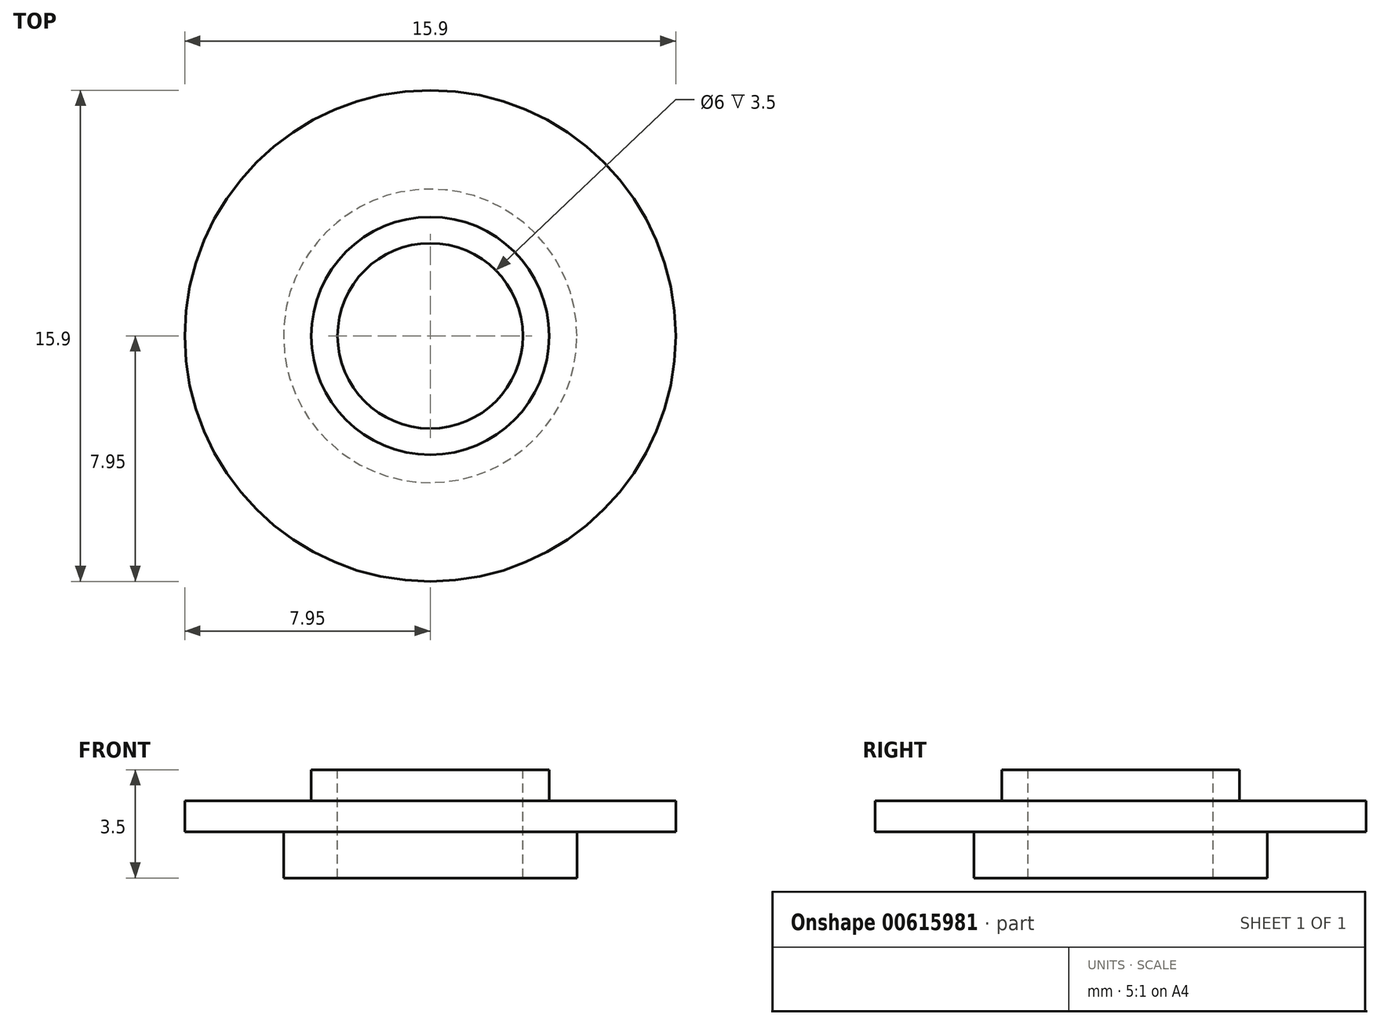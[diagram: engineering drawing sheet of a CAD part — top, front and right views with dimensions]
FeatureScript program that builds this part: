
annotation { "Feature Type Name" : "Feature", "Feature Type Description" : "" }
export const myFeature = defineFeature(function(context is Context, id is Id, definition is map)
    precondition{}
    {
        {
            var Q0;
            Q0=qCreatedBy(makeId("Top.planeOp"),FACE);
            var sketch = newSketch(context, id + "F0", { "sketchPlane" : qUnion([Q0])});
            skCircle(sketch, "E0", {"center": v(0, 0) * mm, "radius": 7.95 * mm});
            skSolve(sketch);
        }
        {
            var Q0;
            Q0=makeQuery(id+"F0.imprint","IMPRINT",FACE,{"disambiguationData":[TD([[makeQuery(id+"F0.imprint","IMPRINT",EDGE,{"derivedFrom":sQuery(id+"F0.wireOp",EDGE,"E0")}),1.0]])]});
            var Q1;
            Q1=sQuery(id+"F0.wireOp",EDGE,"E0");
            extrude(context, id + "F1", {"entities" : qUnion([Q0]), "surfaceEntities" : qUnion([Q1]), "depth" : 1 * mm, "offsetDistance" : 25.4 * mm});
        }
        {
            var Q0;
            Q0=makeQuery(id+"F1.opExtrude","CAP_FACE",FACE,{"disambiguationData":[OSD([sQuery(id+"F0.wireOp",EDGE,"E0")])],"isStart":true});
            var sketch = newSketch(context, id + "F2", { "sketchPlane" : qUnion([Q0])});
            skCircle(sketch, "E1", {"center": v(0, 0) * mm, "radius": 4.75 * mm});
            skSolve(sketch);
        }
        {
            var Q0;
            Q0 = qSketchRegion(id + "F2", true);
            extrude(context, id + "F3", {"entities" : qUnion([Q0]), "operationType" : NewBodyOperationType.ADD, "depth" : 1.5 * mm, "offsetDistance" : 25.4 * mm});
        }
        {
            var Q0;
            Q0=makeQuery(id+"F1.opExtrude","CAP_FACE",FACE,{"disambiguationData":[OSD([sQuery(id+"F0.wireOp",EDGE,"E0")])],"isStart":false});
            var sketch = newSketch(context, id + "F4", { "sketchPlane" : qUnion([Q0])});
            skCircle(sketch, "E2", {"center": v(0, 0) * mm, "radius": 3.85 * mm});
            skSolve(sketch);
        }
        {
            var Q0;
            Q0 = qSketchRegion(id + "F4", true);
            extrude(context, id + "F5", {"entities" : qUnion([Q0]), "operationType" : NewBodyOperationType.ADD, "depth" : 1 * mm, "offsetDistance" : 25.4 * mm});
        }
        {
            var Q0;
            Q0=makeQuery(id+"F5.opExtrude","CAP_FACE",FACE,{"disambiguationData":[OSD([sQuery(id+"F4.wireOp",EDGE,"E2")])],"isStart":false});
            var sketch = newSketch(context, id + "F6", { "sketchPlane" : qUnion([Q0])});
            skCircle(sketch, "E3", {"center": v(0, 0) * mm, "radius": 3 * mm});
            skSolve(sketch);
        }
        {
            var Q0;
            Q0=makeQuery(id+"F6.imprint","IMPRINT",FACE,{"disambiguationData":[TD([[makeQuery(id+"F6.imprint","IMPRINT",EDGE,{"derivedFrom":sQuery(id+"F6.wireOp",EDGE,"E3")}),1.0]])]});
            var Q1;
            Q1=sQuery(id+"F6.wireOp",EDGE,"E3");
            extrude(context, id + "F7", {"entities" : qUnion([Q0]), "operationType" : NewBodyOperationType.REMOVE, "surfaceEntities" : qUnion([Q1]), "oppositeDirection" : true, "depth" : 25.4 * mm, "offsetDistance" : 25.4 * mm});
        }
    });
